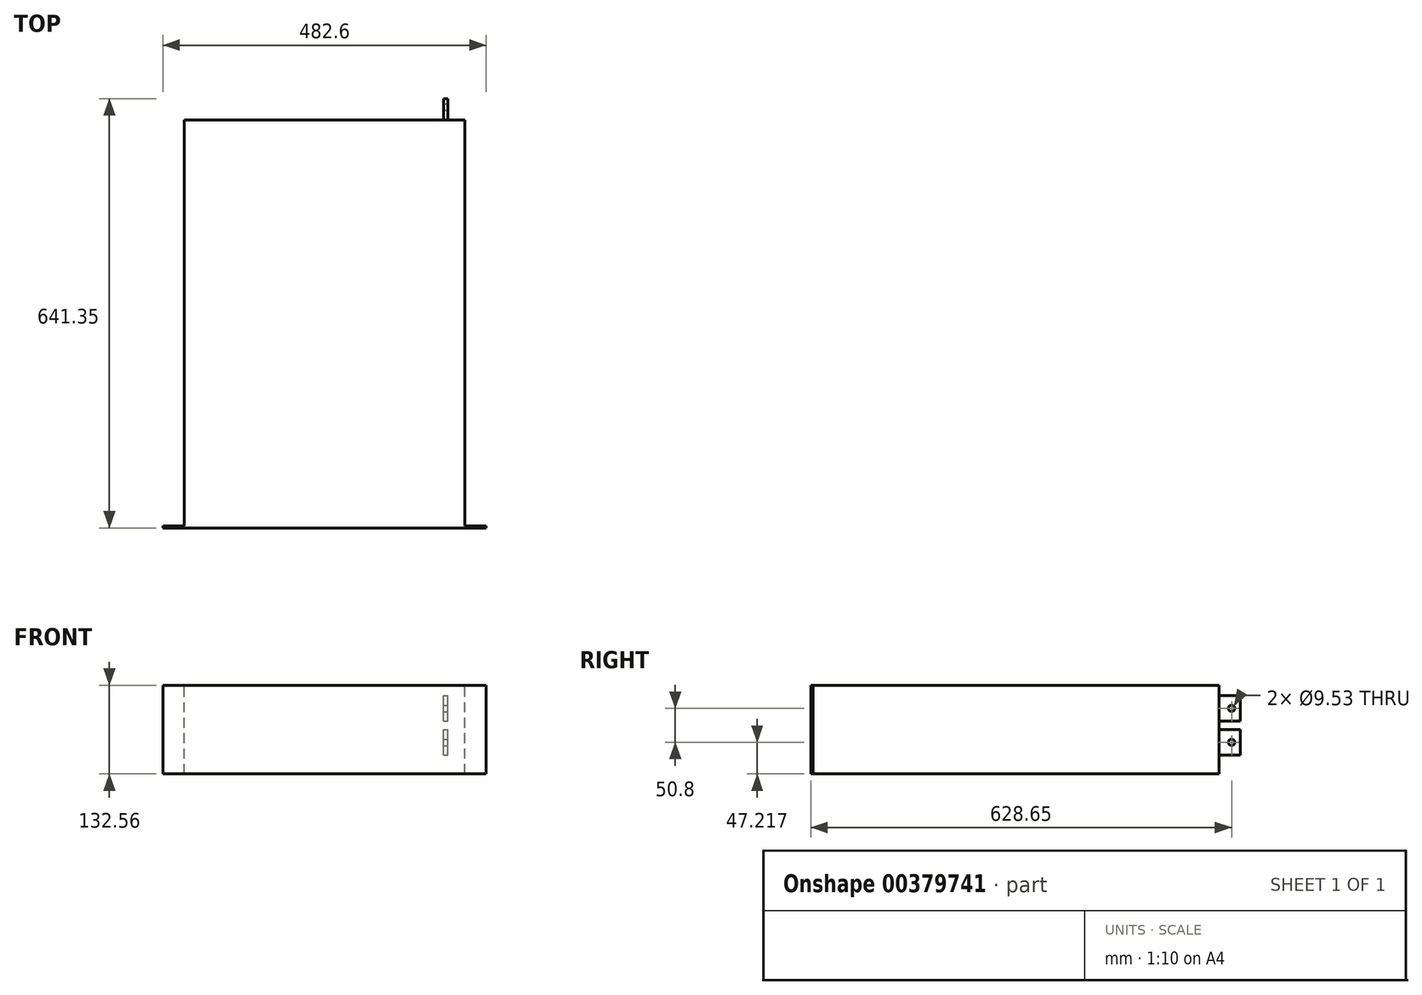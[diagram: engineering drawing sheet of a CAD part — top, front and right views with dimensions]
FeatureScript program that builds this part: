
annotation { "Feature Type Name" : "Feature", "Feature Type Description" : "" }
export const myFeature = defineFeature(function(context is Context, id is Id, definition is map)
    precondition{}
    {
        {
            var Q0;
            Q0=qCreatedBy(makeId("Front.planeOp"),FACE);
            var sketch = newSketch(context, id + "F0", { "sketchPlane" : qUnion([Q0])});
            skLineSegment(sketch, "E0.bottom", {"start": v(241.3, 66.28) * mm, "end": v(-241.3, 66.28) * mm});
            skLineSegment(sketch, "E0.top", {"start": v(241.3, -66.28) * mm, "end": v(-241.3, -66.28) * mm});
            skLineSegment(sketch, "E0.left", {"start": v(241.3, 66.28) * mm, "end": v(241.3, -66.28) * mm});
            skLineSegment(sketch, "E0.right", {"start": v(-241.3, 66.28) * mm, "end": v(-241.3, -66.28) * mm});
            skPoint(sketch, "E0.middle", {"position": v(0, 0) * mm});
            skLineSegment(sketch, "E1", {"start": v(-209.55, 66.28) * mm, "end": v(-209.55, -66.28) * mm});
            skLineSegment(sketch, "E2", {"start": v(209.55, 66.28) * mm, "end": v(209.55, -66.28) * mm});
            skSolve(sketch);
        }
        {
            var Q0;
            {var subQ0=sQuery(id+"F0.wireOp",EDGE,"E1");Q0=makeQuery(id+"F0.imprint","IMPRINT",FACE,{"disambiguationData":[TD([[makeQuery(id+"F0.imprint","IMPRINT",EDGE,{"derivedFrom":subQ0}),1.0]])]});}
            extrude(context, id + "F1", {"entities" : qUnion([Q0]), "oppositeDirection" : true, "depth" : 609.6 * mm});
        }
        {
            var Q0;
            Q0 = qSketchRegion(id + "F0", true);
            extrude(context, id + "F2", {"entities" : qUnion([Q0]), "operationType" : NewBodyOperationType.ADD, "oppositeDirection" : true, "depth" : 3.17 * mm});
        }
        {
            var Q0;
            Q0=makeQuery(id+"F1.opExtrude","CAP_FACE",FACE,{"disambiguationData":[OSD([sQuery(id+"F0.wireOp",EDGE,"E0.bottom"),sQuery(id+"F0.wireOp",EDGE,"E0.top"),sQuery(id+"F0.wireOp",EDGE,"E1"),sQuery(id+"F0.wireOp",EDGE,"E2")])],"isStart":false});
            var sketch = newSketch(context, id + "F3", { "sketchPlane" : qUnion([Q0])});
            skLineSegment(sketch, "E3", {"start": v(-180.97, 75.4) * mm, "end": v(-180.97, -73.62) * mm, "construction": true});
            skLineSegment(sketch, "E4.bottom", {"start": v(-177.8, 12.56) * mm, "end": v(-184.15, 12.56) * mm});
            skLineSegment(sketch, "E4.top", {"start": v(-177.8, 50.91) * mm, "end": v(-184.15, 50.91) * mm});
            skLineSegment(sketch, "E4.left", {"start": v(-177.8, 12.56) * mm, "end": v(-177.8, 50.91) * mm});
            skLineSegment(sketch, "E4.right", {"start": v(-184.15, 12.56) * mm, "end": v(-184.15, 50.91) * mm});
            skPoint(sketch, "E4.middle", {"position": v(-180.97, 31.74) * mm});
            skLineSegment(sketch, "E5.bottom", {"start": v(-177.8, -38.24) * mm, "end": v(-184.15, -38.24) * mm});
            skLineSegment(sketch, "E5.top", {"start": v(-177.8, 0.11) * mm, "end": v(-184.15, 0.11) * mm});
            skLineSegment(sketch, "E5.left", {"start": v(-177.8, -38.24) * mm, "end": v(-177.8, 0.11) * mm});
            skLineSegment(sketch, "E5.right", {"start": v(-184.15, -38.24) * mm, "end": v(-184.15, 0.11) * mm});
            skPoint(sketch, "E5.middle", {"position": v(-180.97, -19.06) * mm});
            skSolve(sketch);
        }
        {
            var Q0;
            Q0=makeQuery(id+"F3.imprint","IMPRINT",FACE,{"disambiguationData":[TD([[makeQuery(id+"F3.imprint","IMPRINT",EDGE,{"derivedFrom":sQuery(id+"F3.wireOp",EDGE,"E4.bottom")}),-1.0]])]});
            var Q1;
            Q1=makeQuery(id+"F3.imprint","IMPRINT",FACE,{"disambiguationData":[TD([[makeQuery(id+"F3.imprint","IMPRINT",EDGE,{"derivedFrom":sQuery(id+"F3.wireOp",EDGE,"E5.bottom")}),-1.0]])]});
            extrude(context, id + "F4", {"entities" : qUnion([Q0, Q1]), "operationType" : NewBodyOperationType.ADD, "depth" : 31.75 * mm});
        }
        {
            var Q0;
            Q0=makeQuery(id+"F4.opExtrude","SWEPT_FACE",FACE,{"disambiguationData":[OSD([sQuery(id+"F3.wireOp",EDGE,"E4.right")])]});
            var sketch = newSketch(context, id + "F5", { "sketchPlane" : qUnion([Q0])});
            skLineSegment(sketch, "E6", {"start": v(628.65, 70.01) * mm, "end": v(628.65, -67.97) * mm, "construction": true});
            skCircle(sketch, "E7", {"center": v(628.65, 31.74) * mm, "radius": 4.76 * mm});
            skCircle(sketch, "E8", {"center": v(628.65, -19.06) * mm, "radius": 4.76 * mm});
            skSolve(sketch);
        }
        {
            var Q0;
            Q0=makeQuery(id+"F5.imprint","IMPRINT",FACE,{"disambiguationData":[TD([[makeQuery(id+"F5.imprint","IMPRINT",EDGE,{"derivedFrom":sQuery(id+"F5.wireOp",EDGE,"E7")}),1.0]])]});
            var Q1;
            Q1=makeQuery(id+"F5.imprint","IMPRINT",FACE,{"disambiguationData":[TD([[makeQuery(id+"F5.imprint","IMPRINT",EDGE,{"derivedFrom":sQuery(id+"F5.wireOp",EDGE,"E8")}),1.0]])]});
            extrude(context, id + "F6", {"entities" : qUnion([Q0, Q1]), "operationType" : NewBodyOperationType.REMOVE, "endBound" : BoundingType.THROUGH_ALL, "oppositeDirection" : true, "depth" : 25.4 * mm});
        }
    });
